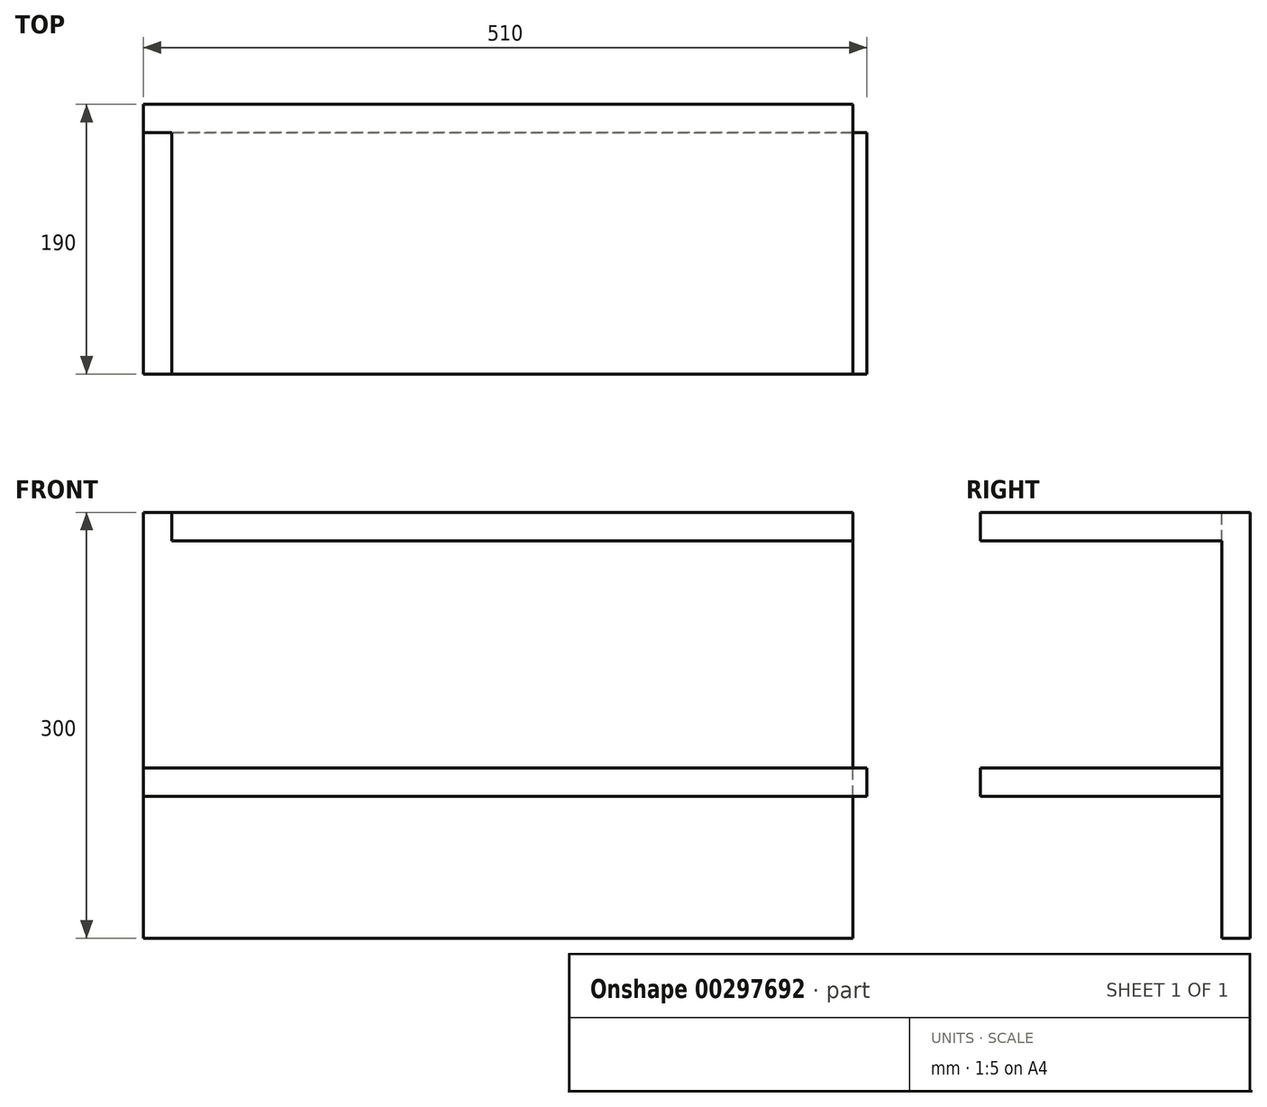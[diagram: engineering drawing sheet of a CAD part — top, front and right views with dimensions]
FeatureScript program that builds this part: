
annotation { "Feature Type Name" : "Feature", "Feature Type Description" : "" }
export const myFeature = defineFeature(function(context is Context, id is Id, definition is map)
    precondition{}
    {
        {
            var Q0;
            Q0=qCreatedBy(makeId("Top.planeOp"),FACE);
            var sketch = newSketch(context, id + "F0", { "sketchPlane" : qUnion([Q0])});
            skLineSegment(sketch, "E0", {"start": v(0, 0) * mm, "end": v(250, 0) * mm, "construction": true});
            skLineSegment(sketch, "E1.bottom", {"start": v(250, 0) * mm, "end": v(-230, 0) * mm});
            skLineSegment(sketch, "E1.top", {"start": v(250, -190) * mm, "end": v(-230, -190) * mm});
            skLineSegment(sketch, "E1.left", {"start": v(250, 0) * mm, "end": v(250, -190) * mm});
            skLineSegment(sketch, "E1.right", {"start": v(-230, 0) * mm, "end": v(-230, -190) * mm});
            skSolve(sketch);
        }
        {
            var Q0;
            Q0=makeQuery(id+"F0.imprint","IMPRINT",FACE,{"disambiguationData":[TD([[makeQuery(id+"F0.imprint","IMPRINT",EDGE,{"derivedFrom":sQuery(id+"F0.wireOp",EDGE,"E1.bottom")}),1.0]])]});
            extrude(context, id + "F1", {"entities" : qUnion([Q0]), "oppositeDirection" : true, "depth" : 20 * mm});
        }
        {
            var Q0;
            Q0=qCreatedBy(makeId("Front.planeOp"),FACE);
            var sketch = newSketch(context, id + "F2", { "sketchPlane" : qUnion([Q0])});
            skLineSegment(sketch, "E2", {"start": v(0, 0) * mm, "end": v(0, -300) * mm, "construction": true});
            skLineSegment(sketch, "E3", {"start": v(0, -300) * mm, "end": v(250, -300) * mm, "construction": true});
            skLineSegment(sketch, "E4", {"start": v(0, 0) * mm, "end": v(-250, 0) * mm, "construction": true});
            skLineSegment(sketch, "E5.bottom", {"start": v(250, -300) * mm, "end": v(-250, -300) * mm});
            skLineSegment(sketch, "E5.top", {"start": v(250, 0) * mm, "end": v(-250, 0) * mm});
            skLineSegment(sketch, "E5.left", {"start": v(250, -300) * mm, "end": v(250, 0) * mm});
            skLineSegment(sketch, "E5.right", {"start": v(-250, -300) * mm, "end": v(-250, 0) * mm});
            skSolve(sketch);
        }
        {
            var Q0;
            Q0=makeQuery(id+"F2.imprint","IMPRINT",FACE,{"disambiguationData":[TD([[makeQuery(id+"F2.imprint","IMPRINT",EDGE,{"derivedFrom":sQuery(id+"F2.wireOp",EDGE,"E5.bottom")}),-1.0]])]});
            extrude(context, id + "F3", {"entities" : qUnion([Q0]), "operationType" : NewBodyOperationType.ADD, "depth" : 20 * mm});
        }
        {
            var Q0;
            Q0=makeQuery(id+"F3.opExtrude","CAP_FACE",FACE,{"disambiguationData":[OSD([sQuery(id+"F2.wireOp",EDGE,"E5.bottom"),sQuery(id+"F2.wireOp",EDGE,"E5.top"),sQuery(id+"F2.wireOp",EDGE,"E5.left"),sQuery(id+"F2.wireOp",EDGE,"E5.right")])],"isStart":false});
            var sketch = newSketch(context, id + "F4", { "sketchPlane" : qUnion([Q0])});
            skLineSegment(sketch, "E6", {"start": v(10, -20) * mm, "end": v(10, -200) * mm, "construction": true});
            skPoint(sketch, "E6.endSnap0", {"position": v(10, -20) * mm});
            skLineSegment(sketch, "E7", {"start": v(10, -200) * mm, "end": v(260, -200) * mm, "construction": true});
            skLineSegment(sketch, "E8.bottom", {"start": v(260, -200) * mm, "end": v(-250, -200) * mm});
            skLineSegment(sketch, "E8.top", {"start": v(260, -180) * mm, "end": v(-250, -180) * mm});
            skLineSegment(sketch, "E8.left", {"start": v(260, -200) * mm, "end": v(260, -180) * mm});
            skLineSegment(sketch, "E8.right", {"start": v(-250, -200) * mm, "end": v(-250, -180) * mm});
            skSolve(sketch);
        }
        {
            var Q0;
            Q0=makeQuery(id+"F4.imprint","IMPRINT",FACE,{"disambiguationData":[TD([[makeQuery(id+"F4.imprint","IMPRINT",EDGE,{"derivedFrom":sQuery(id+"F4.wireOp",EDGE,"E8.bottom")}),-1.0]])]});
            extrude(context, id + "F5", {"entities" : qUnion([Q0]), "operationType" : NewBodyOperationType.ADD, "depth" : 170 * mm});
        }
        {
            var Q0;
            {var subQ0=sQuery(id+"F4.wireOp",EDGE,"E8.top");Q0=makeQuery(id+"F4.imprint","IMPRINT",FACE,{"disambiguationData":[TD([[makeQuery(id+"F4.imprint","IMPRINT",EDGE,{"derivedFrom":subQ0}),-1.0]])]});}
            var sketch = newSketch(context, id + "F6", { "sketchPlane" : qUnion([Q0])});
            skLineSegment(sketch, "E9", {"start": v(0, -20) * mm, "end": v(10, -20) * mm, "construction": true});
            skLineSegment(sketch, "E10", {"start": v(-5, -180) * mm, "end": v(5, -180) * mm, "construction": true});
            skLineSegment(sketch, "E11.bottom", {"start": v(10, -20) * mm, "end": v(-5, -20) * mm});
            skLineSegment(sketch, "E11.top", {"start": v(10, -180) * mm, "end": v(-5, -180) * mm});
            skLineSegment(sketch, "E11.left", {"start": v(10, -20) * mm, "end": v(10, -180) * mm});
            skLineSegment(sketch, "E11.right", {"start": v(-5, -20) * mm, "end": v(-5, -180) * mm});
            skSolve(sketch);
        }
        {
            var Q0;
            Q0=sQuery(id+"F6.wireOp",EDGE,"E11.left");
            var Q1;
            Q1=sQuery(id+"F6.wireOp",EDGE,"E11.right");
            var Q2;
            Q2=sQuery(id+"F6.wireOp",EDGE,"E11.top");
            var Q3;
            Q3=sQuery(id+"F6.wireOp",EDGE,"E11.bottom");
            extrude(context, id + "F7", {"bodyType" : ExtendedToolBodyType.SURFACE, "surfaceEntities" : qUnion([Q0, Q1, Q2, Q3]), "depth" : 170 * mm});
        }
        {
            var Q0;
            {var subQ0=sQuery(id+"F6.wireOp",EDGE,"E11.right");Q0=makeQuery(id+"F6.imprint","IMPRINT",FACE,{"disambiguationData":[TD([[makeQuery(id+"F6.imprint","IMPRINT",EDGE,{"derivedFrom":subQ0}),-1.0]])]});}
            var sketch = newSketch(context, id + "F8", { "sketchPlane" : qUnion([Q0])});
            skLineSegment(sketch, "E12", {"start": v(0, -20) * mm, "end": v(-230, -20) * mm, "construction": true});
            skLineSegment(sketch, "E13", {"start": v(0, -180) * mm, "end": v(-230, -180) * mm, "construction": true});
            skLineSegment(sketch, "E14.bottom", {"start": v(-230, -20) * mm, "end": v(-250, -20) * mm});
            skLineSegment(sketch, "E14.top", {"start": v(-230, -200) * mm, "end": v(-250, -200) * mm});
            skLineSegment(sketch, "E14.left", {"start": v(-230, -20) * mm, "end": v(-230, -200) * mm});
            skLineSegment(sketch, "E14.right", {"start": v(-250, -20) * mm, "end": v(-250, -200) * mm});
            skSolve(sketch);
        }
        {
            var Q0;
            Q0=sQuery(id+"F8.wireOp",EDGE,"E14.left");
            var Q1;
            Q1=sQuery(id+"F8.wireOp",EDGE,"E14.bottom");
            var Q2;
            Q2=sQuery(id+"F8.wireOp",EDGE,"E14.right");
            var Q3;
            Q3=sQuery(id+"F8.wireOp",EDGE,"E14.top");
            extrude(context, id + "F9", {"bodyType" : ExtendedToolBodyType.SURFACE, "surfaceEntities" : qUnion([Q0, Q1, Q2, Q3]), "depth" : 170 * mm});
        }
        {
            var Q0;
            {var subQ0=sQuery(id+"F6.wireOp",EDGE,"E11.left");Q0=makeQuery(id+"F6.imprint","IMPRINT",FACE,{"disambiguationData":[TD([[makeQuery(id+"F6.imprint","IMPRINT",EDGE,{"derivedFrom":subQ0}),1.0]])]});}
            var sketch = newSketch(context, id + "F10", { "sketchPlane" : qUnion([Q0])});
            skLineSegment(sketch, "E15", {"start": v(10, -20) * mm, "end": v(240, -20) * mm});
            skLineSegment(sketch, "E16", {"start": v(5, -180) * mm, "end": v(235, -180) * mm});
            skLineSegment(sketch, "E17.bottom", {"start": v(240, -20) * mm, "end": v(260, -20) * mm});
            skLineSegment(sketch, "E17.top", {"start": v(240, -200) * mm, "end": v(260, -200) * mm});
            skLineSegment(sketch, "E17.left", {"start": v(240, -20) * mm, "end": v(240, -200) * mm});
            skLineSegment(sketch, "E17.right", {"start": v(260, -20) * mm, "end": v(260, -200) * mm});
            skSolve(sketch);
        }
        {
            var Q0;
            Q0=sQuery(id+"F10.wireOp",EDGE,"E17.left");
            var Q1;
            Q1=sQuery(id+"F10.wireOp",EDGE,"E17.right");
            var Q2;
            Q2=sQuery(id+"F10.wireOp",EDGE,"E17.bottom");
            var Q3;
            Q3=sQuery(id+"F10.wireOp",EDGE,"E17.top");
            extrude(context, id + "F11", {"bodyType" : ExtendedToolBodyType.SURFACE, "surfaceEntities" : qUnion([Q0, Q1, Q2, Q3]), "depth" : 170 * mm});
        }
    });
